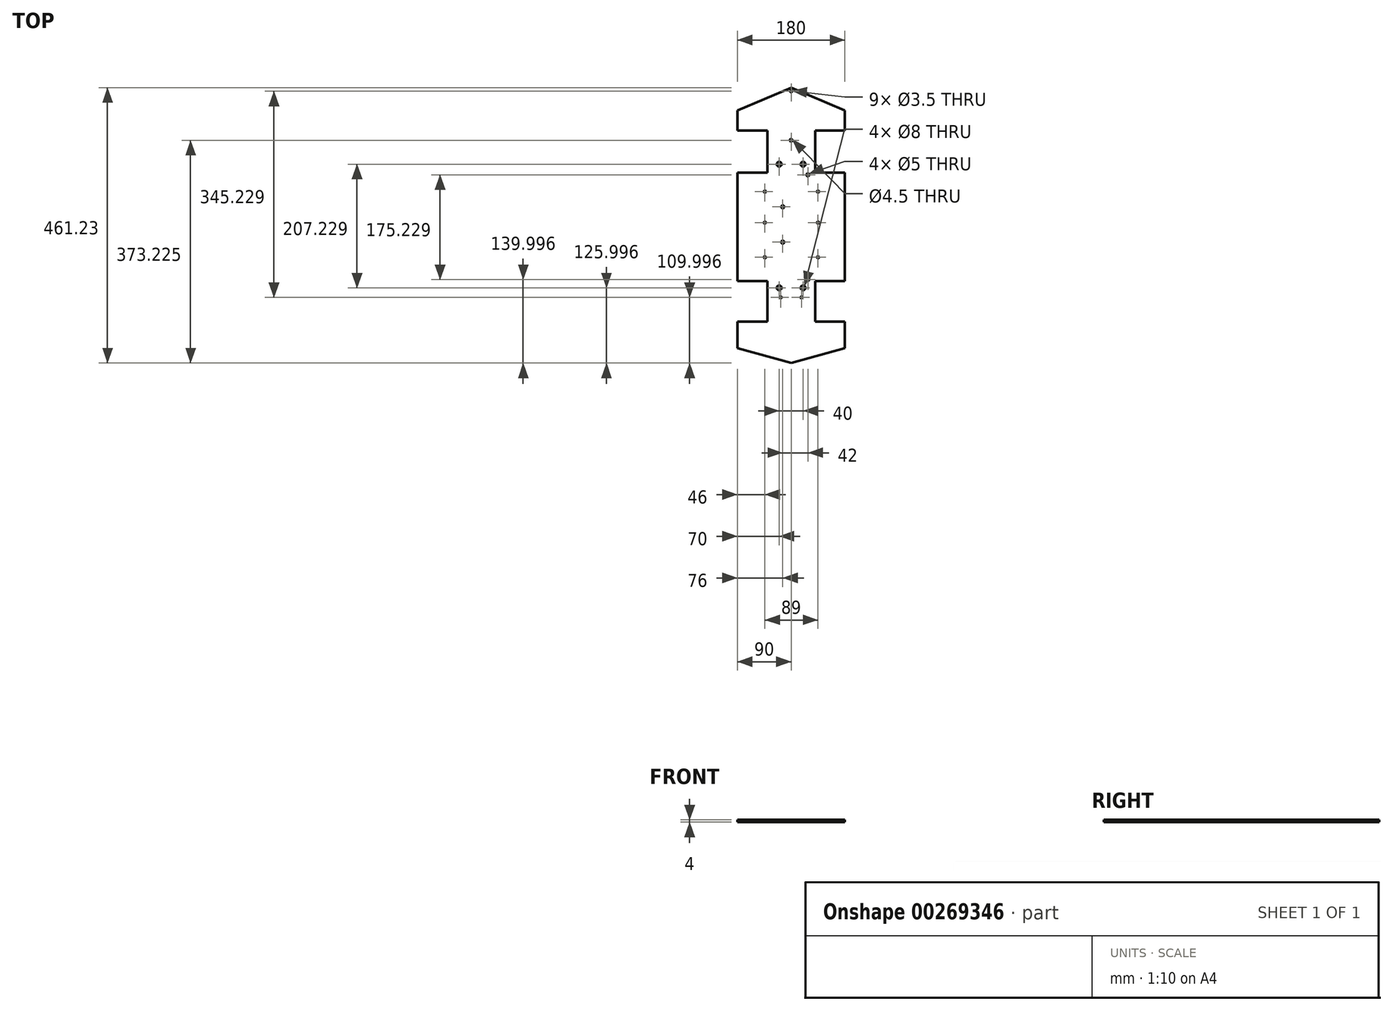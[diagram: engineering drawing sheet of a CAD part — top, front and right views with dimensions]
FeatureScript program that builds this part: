
annotation { "Feature Type Name" : "Feature", "Feature Type Description" : "" }
export const myFeature = defineFeature(function(context is Context, id is Id, definition is map)
    precondition{}
    {
        {
            var Q0;
            Q0=qCreatedBy(makeId("Top.planeOp"),FACE);
            var sketch = newSketch(context, id + "F0", { "sketchPlane" : qUnion([Q0])});
            skLineSegment(sketch, "E0", {"start": v(-90, -39.4) * mm, "end": v(-90, 51.6) * mm});
            skLineSegment(sketch, "E1", {"start": v(-90, -39.4) * mm, "end": v(-90, -130.4) * mm});
            skPoint(sketch, "E2.start.orphan", {"position": v(0, 0) * mm});
            skLineSegment(sketch, "E3", {"start": v(-90, 51.6) * mm, "end": v(-40, 51.6) * mm});
            skLineSegment(sketch, "E4", {"start": v(-40, 51.6) * mm, "end": v(-40, 121.6) * mm});
            skLineSegment(sketch, "E5", {"start": v(-40, 121.6) * mm, "end": v(-90, 121.6) * mm});
            skLineSegment(sketch, "E6", {"start": v(-90, 121.6) * mm, "end": v(-90, 155.6) * mm});
            skPoint(sketch, "E7.end.orphan", {"position": v(0, 220.82) * mm});
            skLineSegment(sketch, "E8", {"start": v(0, 190.54) * mm, "end": v(0, 193.6) * mm});
            skLineSegment(sketch, "E9", {"start": v(-90, 155.6) * mm, "end": v(0, 193.6) * mm});
            skLineSegment(sketch, "E10", {"start": v(-90, -130.4) * mm, "end": v(-40, -130.4) * mm});
            skLineSegment(sketch, "E11", {"start": v(-40, -130.4) * mm, "end": v(-40, -198.4) * mm});
            skLineSegment(sketch, "E12", {"start": v(-40, -198.4) * mm, "end": v(-90, -198.4) * mm});
            skLineSegment(sketch, "E13", {"start": v(-90, -198.4) * mm, "end": v(-90, -242.4) * mm});
            skLineSegment(sketch, "E14", {"start": v(-90, -242.4) * mm, "end": v(0, -267.62) * mm});
            skLineSegment(sketch, "E15", {"start": v(0, 193.6) * mm, "end": v(0, 190.54) * mm});
            skLineSegment(sketch, "E16.MirrorCS", {"start": v(90, 155.6) * mm, "end": v(0, 193.6) * mm});
            skLineSegment(sketch, "E17.MirrorCS", {"start": v(90, 121.6) * mm, "end": v(90, 155.6) * mm});
            skLineSegment(sketch, "E18.MirrorCS", {"start": v(40, 121.6) * mm, "end": v(90, 121.6) * mm});
            skLineSegment(sketch, "E19.MirrorCS", {"start": v(40, 51.6) * mm, "end": v(40, 121.6) * mm});
            skLineSegment(sketch, "E20.MirrorCS", {"start": v(90, 51.6) * mm, "end": v(40, 51.6) * mm});
            skLineSegment(sketch, "E21.MirrorCS", {"start": v(90, -39.4) * mm, "end": v(90, 51.6) * mm});
            skLineSegment(sketch, "E22.MirrorCS", {"start": v(90, -39.4) * mm, "end": v(90, -130.4) * mm});
            skLineSegment(sketch, "E23.MirrorCS", {"start": v(90, -130.4) * mm, "end": v(40, -130.4) * mm});
            skLineSegment(sketch, "E24.MirrorCS", {"start": v(40, -130.4) * mm, "end": v(40, -198.4) * mm});
            skLineSegment(sketch, "E25.MirrorCS", {"start": v(40, -198.4) * mm, "end": v(90, -198.4) * mm});
            skLineSegment(sketch, "E26.MirrorCS", {"start": v(90, -198.4) * mm, "end": v(90, -242.4) * mm});
            skLineSegment(sketch, "E27.MirrorCS", {"start": v(90, -242.4) * mm, "end": v(0, -267.62) * mm});
            skSolve(sketch);
        }
        {
            var Q0;
            Q0=makeQuery(id+"F0.imprint","IMPRINT",FACE,{"disambiguationData":[TD([[makeQuery(id+"F0.imprint","IMPRINT",EDGE,{"derivedFrom":sQuery(id+"F0.wireOp",EDGE,"E0")}),-1.0]])]});
            extrude(context, id + "F1", {"entities" : qUnion([Q0]), "depth" : 4 * mm});
        }
        {
            var Q0;
            Q0=makeQuery(id+"F1.opExtrude","CAP_FACE",FACE,{"disambiguationData":[OSD([sQuery(id+"F0.wireOp",EDGE,"E0"),sQuery(id+"F0.wireOp",EDGE,"E1"),sQuery(id+"F0.wireOp",EDGE,"E3"),sQuery(id+"F0.wireOp",EDGE,"E4"),sQuery(id+"F0.wireOp",EDGE,"E5"),sQuery(id+"F0.wireOp",EDGE,"E6"),sQuery(id+"F0.wireOp",EDGE,"E9"),sQuery(id+"F0.wireOp",EDGE,"E10"),sQuery(id+"F0.wireOp",EDGE,"E11"),sQuery(id+"F0.wireOp",EDGE,"E12"),sQuery(id+"F0.wireOp",EDGE,"E13"),sQuery(id+"F0.wireOp",EDGE,"E14"),sQuery(id+"F0.wireOp",EDGE,"E16.MirrorCS"),sQuery(id+"F0.wireOp",EDGE,"E17.MirrorCS"),sQuery(id+"F0.wireOp",EDGE,"E18.MirrorCS"),sQuery(id+"F0.wireOp",EDGE,"E19.MirrorCS"),sQuery(id+"F0.wireOp",EDGE,"E20.MirrorCS"),sQuery(id+"F0.wireOp",EDGE,"E21.MirrorCS"),sQuery(id+"F0.wireOp",EDGE,"E22.MirrorCS"),sQuery(id+"F0.wireOp",EDGE,"E23.MirrorCS"),sQuery(id+"F0.wireOp",EDGE,"E24.MirrorCS"),sQuery(id+"F0.wireOp",EDGE,"E25.MirrorCS"),sQuery(id+"F0.wireOp",EDGE,"E26.MirrorCS"),sQuery(id+"F0.wireOp",EDGE,"E27.MirrorCS")])],"isStart":false});
            var sketch = newSketch(context, id + "F2", { "sketchPlane" : qUnion([Q0])});
            skLineSegment(sketch, "E28", {"start": v(0, 193.6) * mm, "end": v(0, -267.62) * mm});
            skCircle(sketch, "E29", {"center": v(0, 187.6) * mm, "radius": 12.42 * mm});
            skSolve(sketch);
        }
        {
            var Q0;
            Q0=sQuery(id+"F2.wireOp",VERTEX,"E29.center");
            var Q1;
            Q1=makeQuery(id+"F1.opExtrude","SWEPT_BODY",BODY,{"disambiguationData":[OSD([sQuery(id+"F0.wireOp",EDGE,"E0"),sQuery(id+"F0.wireOp",EDGE,"E1"),sQuery(id+"F0.wireOp",EDGE,"E3"),sQuery(id+"F0.wireOp",EDGE,"E4"),sQuery(id+"F0.wireOp",EDGE,"E5"),sQuery(id+"F0.wireOp",EDGE,"E6"),sQuery(id+"F0.wireOp",EDGE,"E9"),sQuery(id+"F0.wireOp",EDGE,"E10"),sQuery(id+"F0.wireOp",EDGE,"E11"),sQuery(id+"F0.wireOp",EDGE,"E12"),sQuery(id+"F0.wireOp",EDGE,"E13"),sQuery(id+"F0.wireOp",EDGE,"E14"),sQuery(id+"F0.wireOp",EDGE,"E16.MirrorCS"),sQuery(id+"F0.wireOp",EDGE,"E17.MirrorCS"),sQuery(id+"F0.wireOp",EDGE,"E18.MirrorCS"),sQuery(id+"F0.wireOp",EDGE,"E19.MirrorCS"),sQuery(id+"F0.wireOp",EDGE,"E20.MirrorCS"),sQuery(id+"F0.wireOp",EDGE,"E21.MirrorCS"),sQuery(id+"F0.wireOp",EDGE,"E22.MirrorCS"),sQuery(id+"F0.wireOp",EDGE,"E23.MirrorCS"),sQuery(id+"F0.wireOp",EDGE,"E24.MirrorCS"),sQuery(id+"F0.wireOp",EDGE,"E25.MirrorCS"),sQuery(id+"F0.wireOp",EDGE,"E26.MirrorCS"),sQuery(id+"F0.wireOp",EDGE,"E27.MirrorCS")])]});
            hole(context, id + "F3", {"style" : HoleStyle.SIMPLE, "endStyle" : HoleEndStyle.BLIND, "holeDiameter" : 3.5 * mm, "holeDepth" : 4 * mm, "tappedDepth" : 12 * mm, "tapClearance" : 3, "startFromSketch" : true, "locations" : qUnion([Q0]), "scope" : qUnion([Q1])});
        }
        {
            var Q0;
            Q0=makeQuery(id+"F1.opExtrude","CAP_FACE",FACE,{"disambiguationData":[OSD([sQuery(id+"F0.wireOp",EDGE,"E0"),sQuery(id+"F0.wireOp",EDGE,"E1"),sQuery(id+"F0.wireOp",EDGE,"E3"),sQuery(id+"F0.wireOp",EDGE,"E4"),sQuery(id+"F0.wireOp",EDGE,"E5"),sQuery(id+"F0.wireOp",EDGE,"E6"),sQuery(id+"F0.wireOp",EDGE,"E9"),sQuery(id+"F0.wireOp",EDGE,"E10"),sQuery(id+"F0.wireOp",EDGE,"E11"),sQuery(id+"F0.wireOp",EDGE,"E12"),sQuery(id+"F0.wireOp",EDGE,"E13"),sQuery(id+"F0.wireOp",EDGE,"E14"),sQuery(id+"F0.wireOp",EDGE,"E16.MirrorCS"),sQuery(id+"F0.wireOp",EDGE,"E17.MirrorCS"),sQuery(id+"F0.wireOp",EDGE,"E18.MirrorCS"),sQuery(id+"F0.wireOp",EDGE,"E19.MirrorCS"),sQuery(id+"F0.wireOp",EDGE,"E20.MirrorCS"),sQuery(id+"F0.wireOp",EDGE,"E21.MirrorCS"),sQuery(id+"F0.wireOp",EDGE,"E22.MirrorCS"),sQuery(id+"F0.wireOp",EDGE,"E23.MirrorCS"),sQuery(id+"F0.wireOp",EDGE,"E24.MirrorCS"),sQuery(id+"F0.wireOp",EDGE,"E25.MirrorCS"),sQuery(id+"F0.wireOp",EDGE,"E26.MirrorCS"),sQuery(id+"F0.wireOp",EDGE,"E27.MirrorCS")])],"isStart":false});
            var sketch = newSketch(context, id + "F4", { "sketchPlane" : qUnion([Q0])});
            skLineSegment(sketch, "E30", {"start": v(0, 193.6) * mm, "end": v(0, -267.62) * mm});
            skCircle(sketch, "E31", {"center": v(0, 105.6) * mm, "radius": 11.78 * mm});
            skSolve(sketch);
        }
        {
            var Q0;
            Q0=sQuery(id+"F4.wireOp",VERTEX,"E31.center");
            var Q1;
            Q1=makeQuery(id+"F1.opExtrude","SWEPT_BODY",BODY,{"disambiguationData":[OSD([sQuery(id+"F0.wireOp",EDGE,"E0"),sQuery(id+"F0.wireOp",EDGE,"E1"),sQuery(id+"F0.wireOp",EDGE,"E3"),sQuery(id+"F0.wireOp",EDGE,"E4"),sQuery(id+"F0.wireOp",EDGE,"E5"),sQuery(id+"F0.wireOp",EDGE,"E6"),sQuery(id+"F0.wireOp",EDGE,"E9"),sQuery(id+"F0.wireOp",EDGE,"E10"),sQuery(id+"F0.wireOp",EDGE,"E11"),sQuery(id+"F0.wireOp",EDGE,"E12"),sQuery(id+"F0.wireOp",EDGE,"E13"),sQuery(id+"F0.wireOp",EDGE,"E14"),sQuery(id+"F0.wireOp",EDGE,"E16.MirrorCS"),sQuery(id+"F0.wireOp",EDGE,"E17.MirrorCS"),sQuery(id+"F0.wireOp",EDGE,"E18.MirrorCS"),sQuery(id+"F0.wireOp",EDGE,"E19.MirrorCS"),sQuery(id+"F0.wireOp",EDGE,"E20.MirrorCS"),sQuery(id+"F0.wireOp",EDGE,"E21.MirrorCS"),sQuery(id+"F0.wireOp",EDGE,"E22.MirrorCS"),sQuery(id+"F0.wireOp",EDGE,"E23.MirrorCS"),sQuery(id+"F0.wireOp",EDGE,"E24.MirrorCS"),sQuery(id+"F0.wireOp",EDGE,"E25.MirrorCS"),sQuery(id+"F0.wireOp",EDGE,"E26.MirrorCS"),sQuery(id+"F0.wireOp",EDGE,"E27.MirrorCS")])]});
            hole(context, id + "F5", {"style" : HoleStyle.SIMPLE, "endStyle" : HoleEndStyle.BLIND, "holeDiameter" : 4.5 * mm, "holeDepth" : 4 * mm, "tappedDepth" : 12 * mm, "tapClearance" : 3, "startFromSketch" : true, "locations" : qUnion([Q0]), "scope" : qUnion([Q1])});
        }
        {
            var Q0;
            Q0=makeQuery(id+"F1.opExtrude","CAP_FACE",FACE,{"disambiguationData":[OSD([sQuery(id+"F0.wireOp",EDGE,"E0"),sQuery(id+"F0.wireOp",EDGE,"E1"),sQuery(id+"F0.wireOp",EDGE,"E3"),sQuery(id+"F0.wireOp",EDGE,"E4"),sQuery(id+"F0.wireOp",EDGE,"E5"),sQuery(id+"F0.wireOp",EDGE,"E6"),sQuery(id+"F0.wireOp",EDGE,"E9"),sQuery(id+"F0.wireOp",EDGE,"E10"),sQuery(id+"F0.wireOp",EDGE,"E11"),sQuery(id+"F0.wireOp",EDGE,"E12"),sQuery(id+"F0.wireOp",EDGE,"E13"),sQuery(id+"F0.wireOp",EDGE,"E14"),sQuery(id+"F0.wireOp",EDGE,"E16.MirrorCS"),sQuery(id+"F0.wireOp",EDGE,"E17.MirrorCS"),sQuery(id+"F0.wireOp",EDGE,"E18.MirrorCS"),sQuery(id+"F0.wireOp",EDGE,"E19.MirrorCS"),sQuery(id+"F0.wireOp",EDGE,"E20.MirrorCS"),sQuery(id+"F0.wireOp",EDGE,"E21.MirrorCS"),sQuery(id+"F0.wireOp",EDGE,"E22.MirrorCS"),sQuery(id+"F0.wireOp",EDGE,"E23.MirrorCS"),sQuery(id+"F0.wireOp",EDGE,"E24.MirrorCS"),sQuery(id+"F0.wireOp",EDGE,"E25.MirrorCS"),sQuery(id+"F0.wireOp",EDGE,"E26.MirrorCS"),sQuery(id+"F0.wireOp",EDGE,"E27.MirrorCS")])],"isStart":false});
            var sketch = newSketch(context, id + "F6", { "sketchPlane" : qUnion([Q0])});
            skLineSegment(sketch, "E32", {"start": v(0, 193.6) * mm, "end": v(0, -267.62) * mm});
            skCircle(sketch, "E33", {"center": v(-20, 65.6) * mm, "radius": 13.57 * mm});
            skSolve(sketch);
        }
        {
            var Q0;
            Q0=sQuery(id+"F6.wireOp",VERTEX,"E33.center");
            var Q1;
            Q1=makeQuery(id+"F1.opExtrude","SWEPT_BODY",BODY,{"disambiguationData":[OSD([sQuery(id+"F0.wireOp",EDGE,"E0"),sQuery(id+"F0.wireOp",EDGE,"E1"),sQuery(id+"F0.wireOp",EDGE,"E3"),sQuery(id+"F0.wireOp",EDGE,"E4"),sQuery(id+"F0.wireOp",EDGE,"E5"),sQuery(id+"F0.wireOp",EDGE,"E6"),sQuery(id+"F0.wireOp",EDGE,"E9"),sQuery(id+"F0.wireOp",EDGE,"E10"),sQuery(id+"F0.wireOp",EDGE,"E11"),sQuery(id+"F0.wireOp",EDGE,"E12"),sQuery(id+"F0.wireOp",EDGE,"E13"),sQuery(id+"F0.wireOp",EDGE,"E14"),sQuery(id+"F0.wireOp",EDGE,"E16.MirrorCS"),sQuery(id+"F0.wireOp",EDGE,"E17.MirrorCS"),sQuery(id+"F0.wireOp",EDGE,"E18.MirrorCS"),sQuery(id+"F0.wireOp",EDGE,"E19.MirrorCS"),sQuery(id+"F0.wireOp",EDGE,"E20.MirrorCS"),sQuery(id+"F0.wireOp",EDGE,"E21.MirrorCS"),sQuery(id+"F0.wireOp",EDGE,"E22.MirrorCS"),sQuery(id+"F0.wireOp",EDGE,"E23.MirrorCS"),sQuery(id+"F0.wireOp",EDGE,"E24.MirrorCS"),sQuery(id+"F0.wireOp",EDGE,"E25.MirrorCS"),sQuery(id+"F0.wireOp",EDGE,"E26.MirrorCS"),sQuery(id+"F0.wireOp",EDGE,"E27.MirrorCS")])]});
            hole(context, id + "F7", {"style" : HoleStyle.SIMPLE, "endStyle" : HoleEndStyle.BLIND, "holeDiameter" : 8 * mm, "holeDepth" : 4 * mm, "tappedDepth" : 12 * mm, "tapClearance" : 3, "startFromSketch" : true, "locations" : qUnion([Q0]), "scope" : qUnion([Q1])});
        }
        {
            var Q0;
            Q0=makeQuery(id+"F1.opExtrude","CAP_FACE",FACE,{"disambiguationData":[OSD([sQuery(id+"F0.wireOp",EDGE,"E0"),sQuery(id+"F0.wireOp",EDGE,"E1"),sQuery(id+"F0.wireOp",EDGE,"E3"),sQuery(id+"F0.wireOp",EDGE,"E4"),sQuery(id+"F0.wireOp",EDGE,"E5"),sQuery(id+"F0.wireOp",EDGE,"E6"),sQuery(id+"F0.wireOp",EDGE,"E9"),sQuery(id+"F0.wireOp",EDGE,"E10"),sQuery(id+"F0.wireOp",EDGE,"E11"),sQuery(id+"F0.wireOp",EDGE,"E12"),sQuery(id+"F0.wireOp",EDGE,"E13"),sQuery(id+"F0.wireOp",EDGE,"E14"),sQuery(id+"F0.wireOp",EDGE,"E16.MirrorCS"),sQuery(id+"F0.wireOp",EDGE,"E17.MirrorCS"),sQuery(id+"F0.wireOp",EDGE,"E18.MirrorCS"),sQuery(id+"F0.wireOp",EDGE,"E19.MirrorCS"),sQuery(id+"F0.wireOp",EDGE,"E20.MirrorCS"),sQuery(id+"F0.wireOp",EDGE,"E21.MirrorCS"),sQuery(id+"F0.wireOp",EDGE,"E22.MirrorCS"),sQuery(id+"F0.wireOp",EDGE,"E23.MirrorCS"),sQuery(id+"F0.wireOp",EDGE,"E24.MirrorCS"),sQuery(id+"F0.wireOp",EDGE,"E25.MirrorCS"),sQuery(id+"F0.wireOp",EDGE,"E26.MirrorCS"),sQuery(id+"F0.wireOp",EDGE,"E27.MirrorCS")])],"isStart":false});
            var sketch = newSketch(context, id + "F8", { "sketchPlane" : qUnion([Q0])});
            skLineSegment(sketch, "E34", {"start": v(0, 193.6) * mm, "end": v(0, -267.62) * mm});
            skCircle(sketch, "E35", {"center": v(20, 65.6) * mm, "radius": 14.44 * mm});
            skSolve(sketch);
        }
        {
            var Q0;
            Q0=sQuery(id+"F8.wireOp",VERTEX,"E35.center");
            var Q1;
            Q1=makeQuery(id+"F1.opExtrude","SWEPT_BODY",BODY,{"disambiguationData":[OSD([sQuery(id+"F0.wireOp",EDGE,"E0"),sQuery(id+"F0.wireOp",EDGE,"E1"),sQuery(id+"F0.wireOp",EDGE,"E3"),sQuery(id+"F0.wireOp",EDGE,"E4"),sQuery(id+"F0.wireOp",EDGE,"E5"),sQuery(id+"F0.wireOp",EDGE,"E6"),sQuery(id+"F0.wireOp",EDGE,"E9"),sQuery(id+"F0.wireOp",EDGE,"E10"),sQuery(id+"F0.wireOp",EDGE,"E11"),sQuery(id+"F0.wireOp",EDGE,"E12"),sQuery(id+"F0.wireOp",EDGE,"E13"),sQuery(id+"F0.wireOp",EDGE,"E14"),sQuery(id+"F0.wireOp",EDGE,"E16.MirrorCS"),sQuery(id+"F0.wireOp",EDGE,"E17.MirrorCS"),sQuery(id+"F0.wireOp",EDGE,"E18.MirrorCS"),sQuery(id+"F0.wireOp",EDGE,"E19.MirrorCS"),sQuery(id+"F0.wireOp",EDGE,"E20.MirrorCS"),sQuery(id+"F0.wireOp",EDGE,"E21.MirrorCS"),sQuery(id+"F0.wireOp",EDGE,"E22.MirrorCS"),sQuery(id+"F0.wireOp",EDGE,"E23.MirrorCS"),sQuery(id+"F0.wireOp",EDGE,"E24.MirrorCS"),sQuery(id+"F0.wireOp",EDGE,"E25.MirrorCS"),sQuery(id+"F0.wireOp",EDGE,"E26.MirrorCS"),sQuery(id+"F0.wireOp",EDGE,"E27.MirrorCS")])]});
            hole(context, id + "F9", {"style" : HoleStyle.SIMPLE, "endStyle" : HoleEndStyle.BLIND, "holeDiameter" : 8 * mm, "holeDepth" : 4 * mm, "tappedDepth" : 12 * mm, "tapClearance" : 3, "startFromSketch" : true, "locations" : qUnion([Q0]), "scope" : qUnion([Q1])});
        }
        {
            var Q0;
            Q0=makeQuery(id+"F1.opExtrude","CAP_FACE",FACE,{"disambiguationData":[OSD([sQuery(id+"F0.wireOp",EDGE,"E0"),sQuery(id+"F0.wireOp",EDGE,"E1"),sQuery(id+"F0.wireOp",EDGE,"E3"),sQuery(id+"F0.wireOp",EDGE,"E4"),sQuery(id+"F0.wireOp",EDGE,"E5"),sQuery(id+"F0.wireOp",EDGE,"E6"),sQuery(id+"F0.wireOp",EDGE,"E9"),sQuery(id+"F0.wireOp",EDGE,"E10"),sQuery(id+"F0.wireOp",EDGE,"E11"),sQuery(id+"F0.wireOp",EDGE,"E12"),sQuery(id+"F0.wireOp",EDGE,"E13"),sQuery(id+"F0.wireOp",EDGE,"E14"),sQuery(id+"F0.wireOp",EDGE,"E16.MirrorCS"),sQuery(id+"F0.wireOp",EDGE,"E17.MirrorCS"),sQuery(id+"F0.wireOp",EDGE,"E18.MirrorCS"),sQuery(id+"F0.wireOp",EDGE,"E19.MirrorCS"),sQuery(id+"F0.wireOp",EDGE,"E20.MirrorCS"),sQuery(id+"F0.wireOp",EDGE,"E21.MirrorCS"),sQuery(id+"F0.wireOp",EDGE,"E22.MirrorCS"),sQuery(id+"F0.wireOp",EDGE,"E23.MirrorCS"),sQuery(id+"F0.wireOp",EDGE,"E24.MirrorCS"),sQuery(id+"F0.wireOp",EDGE,"E25.MirrorCS"),sQuery(id+"F0.wireOp",EDGE,"E26.MirrorCS"),sQuery(id+"F0.wireOp",EDGE,"E27.MirrorCS")])],"isStart":false});
            var sketch = newSketch(context, id + "F10", { "sketchPlane" : qUnion([Q0])});
            skLineSegment(sketch, "E36", {"start": v(0, 193.6) * mm, "end": v(0, -267.62) * mm});
            skCircle(sketch, "E37", {"center": v(28, 47.6) * mm, "radius": 46 * mm});
            skSolve(sketch);
        }
        {
            var Q0;
            Q0=sQuery(id+"F10.wireOp",VERTEX,"E37.center");
            var Q1;
            Q1=makeQuery(id+"F1.opExtrude","SWEPT_BODY",BODY,{"disambiguationData":[OSD([sQuery(id+"F0.wireOp",EDGE,"E0"),sQuery(id+"F0.wireOp",EDGE,"E1"),sQuery(id+"F0.wireOp",EDGE,"E3"),sQuery(id+"F0.wireOp",EDGE,"E4"),sQuery(id+"F0.wireOp",EDGE,"E5"),sQuery(id+"F0.wireOp",EDGE,"E6"),sQuery(id+"F0.wireOp",EDGE,"E9"),sQuery(id+"F0.wireOp",EDGE,"E10"),sQuery(id+"F0.wireOp",EDGE,"E11"),sQuery(id+"F0.wireOp",EDGE,"E12"),sQuery(id+"F0.wireOp",EDGE,"E13"),sQuery(id+"F0.wireOp",EDGE,"E14"),sQuery(id+"F0.wireOp",EDGE,"E16.MirrorCS"),sQuery(id+"F0.wireOp",EDGE,"E17.MirrorCS"),sQuery(id+"F0.wireOp",EDGE,"E18.MirrorCS"),sQuery(id+"F0.wireOp",EDGE,"E19.MirrorCS"),sQuery(id+"F0.wireOp",EDGE,"E20.MirrorCS"),sQuery(id+"F0.wireOp",EDGE,"E21.MirrorCS"),sQuery(id+"F0.wireOp",EDGE,"E22.MirrorCS"),sQuery(id+"F0.wireOp",EDGE,"E23.MirrorCS"),sQuery(id+"F0.wireOp",EDGE,"E24.MirrorCS"),sQuery(id+"F0.wireOp",EDGE,"E25.MirrorCS"),sQuery(id+"F0.wireOp",EDGE,"E26.MirrorCS"),sQuery(id+"F0.wireOp",EDGE,"E27.MirrorCS")])]});
            hole(context, id + "F11", {"style" : HoleStyle.SIMPLE, "endStyle" : HoleEndStyle.BLIND, "holeDiameter" : 5 * mm, "holeDepth" : 4 * mm, "tappedDepth" : 12 * mm, "tapClearance" : 3, "startFromSketch" : true, "locations" : qUnion([Q0]), "scope" : qUnion([Q1])});
        }
        {
            var Q0;
            Q0=makeQuery(id+"F1.opExtrude","CAP_FACE",FACE,{"disambiguationData":[OSD([sQuery(id+"F0.wireOp",EDGE,"E0"),sQuery(id+"F0.wireOp",EDGE,"E1"),sQuery(id+"F0.wireOp",EDGE,"E3"),sQuery(id+"F0.wireOp",EDGE,"E4"),sQuery(id+"F0.wireOp",EDGE,"E5"),sQuery(id+"F0.wireOp",EDGE,"E6"),sQuery(id+"F0.wireOp",EDGE,"E9"),sQuery(id+"F0.wireOp",EDGE,"E10"),sQuery(id+"F0.wireOp",EDGE,"E11"),sQuery(id+"F0.wireOp",EDGE,"E12"),sQuery(id+"F0.wireOp",EDGE,"E13"),sQuery(id+"F0.wireOp",EDGE,"E14"),sQuery(id+"F0.wireOp",EDGE,"E16.MirrorCS"),sQuery(id+"F0.wireOp",EDGE,"E17.MirrorCS"),sQuery(id+"F0.wireOp",EDGE,"E18.MirrorCS"),sQuery(id+"F0.wireOp",EDGE,"E19.MirrorCS"),sQuery(id+"F0.wireOp",EDGE,"E20.MirrorCS"),sQuery(id+"F0.wireOp",EDGE,"E21.MirrorCS"),sQuery(id+"F0.wireOp",EDGE,"E22.MirrorCS"),sQuery(id+"F0.wireOp",EDGE,"E23.MirrorCS"),sQuery(id+"F0.wireOp",EDGE,"E24.MirrorCS"),sQuery(id+"F0.wireOp",EDGE,"E25.MirrorCS"),sQuery(id+"F0.wireOp",EDGE,"E26.MirrorCS"),sQuery(id+"F0.wireOp",EDGE,"E27.MirrorCS")])],"isStart":false});
            var sketch = newSketch(context, id + "F12", { "sketchPlane" : qUnion([Q0])});
            skLineSegment(sketch, "E38", {"start": v(0, 193.6) * mm, "end": v(0, -267.62) * mm});
            skCircle(sketch, "E39", {"center": v(45, 19.6) * mm, "radius": 21.54 * mm});
            skSolve(sketch);
        }
        {
            var Q0;
            Q0=sQuery(id+"F12.wireOp",VERTEX,"E39.center");
            var Q1;
            Q1=makeQuery(id+"F1.opExtrude","SWEPT_BODY",BODY,{"disambiguationData":[OSD([sQuery(id+"F0.wireOp",EDGE,"E0"),sQuery(id+"F0.wireOp",EDGE,"E1"),sQuery(id+"F0.wireOp",EDGE,"E3"),sQuery(id+"F0.wireOp",EDGE,"E4"),sQuery(id+"F0.wireOp",EDGE,"E5"),sQuery(id+"F0.wireOp",EDGE,"E6"),sQuery(id+"F0.wireOp",EDGE,"E9"),sQuery(id+"F0.wireOp",EDGE,"E10"),sQuery(id+"F0.wireOp",EDGE,"E11"),sQuery(id+"F0.wireOp",EDGE,"E12"),sQuery(id+"F0.wireOp",EDGE,"E13"),sQuery(id+"F0.wireOp",EDGE,"E14"),sQuery(id+"F0.wireOp",EDGE,"E16.MirrorCS"),sQuery(id+"F0.wireOp",EDGE,"E17.MirrorCS"),sQuery(id+"F0.wireOp",EDGE,"E18.MirrorCS"),sQuery(id+"F0.wireOp",EDGE,"E19.MirrorCS"),sQuery(id+"F0.wireOp",EDGE,"E20.MirrorCS"),sQuery(id+"F0.wireOp",EDGE,"E21.MirrorCS"),sQuery(id+"F0.wireOp",EDGE,"E22.MirrorCS"),sQuery(id+"F0.wireOp",EDGE,"E23.MirrorCS"),sQuery(id+"F0.wireOp",EDGE,"E24.MirrorCS"),sQuery(id+"F0.wireOp",EDGE,"E25.MirrorCS"),sQuery(id+"F0.wireOp",EDGE,"E26.MirrorCS"),sQuery(id+"F0.wireOp",EDGE,"E27.MirrorCS")])]});
            hole(context, id + "F13", {"style" : HoleStyle.SIMPLE, "endStyle" : HoleEndStyle.BLIND, "holeDiameter" : 3.5 * mm, "holeDepth" : 4 * mm, "tappedDepth" : 12 * mm, "tapClearance" : 3, "startFromSketch" : true, "locations" : qUnion([Q0]), "scope" : qUnion([Q1])});
        }
        {
            var Q0;
            Q0=makeQuery(id+"F1.opExtrude","CAP_FACE",FACE,{"disambiguationData":[OSD([sQuery(id+"F0.wireOp",EDGE,"E0"),sQuery(id+"F0.wireOp",EDGE,"E1"),sQuery(id+"F0.wireOp",EDGE,"E3"),sQuery(id+"F0.wireOp",EDGE,"E4"),sQuery(id+"F0.wireOp",EDGE,"E5"),sQuery(id+"F0.wireOp",EDGE,"E6"),sQuery(id+"F0.wireOp",EDGE,"E9"),sQuery(id+"F0.wireOp",EDGE,"E10"),sQuery(id+"F0.wireOp",EDGE,"E11"),sQuery(id+"F0.wireOp",EDGE,"E12"),sQuery(id+"F0.wireOp",EDGE,"E13"),sQuery(id+"F0.wireOp",EDGE,"E14"),sQuery(id+"F0.wireOp",EDGE,"E16.MirrorCS"),sQuery(id+"F0.wireOp",EDGE,"E17.MirrorCS"),sQuery(id+"F0.wireOp",EDGE,"E18.MirrorCS"),sQuery(id+"F0.wireOp",EDGE,"E19.MirrorCS"),sQuery(id+"F0.wireOp",EDGE,"E20.MirrorCS"),sQuery(id+"F0.wireOp",EDGE,"E21.MirrorCS"),sQuery(id+"F0.wireOp",EDGE,"E22.MirrorCS"),sQuery(id+"F0.wireOp",EDGE,"E23.MirrorCS"),sQuery(id+"F0.wireOp",EDGE,"E24.MirrorCS"),sQuery(id+"F0.wireOp",EDGE,"E25.MirrorCS"),sQuery(id+"F0.wireOp",EDGE,"E26.MirrorCS"),sQuery(id+"F0.wireOp",EDGE,"E27.MirrorCS")])],"isStart":false});
            var sketch = newSketch(context, id + "F14", { "sketchPlane" : qUnion([Q0])});
            skLineSegment(sketch, "E40", {"start": v(0, 193.6) * mm, "end": v(0, -267.62) * mm});
            skCircle(sketch, "E41", {"center": v(45, -32.4) * mm, "radius": 23.3 * mm});
            skSolve(sketch);
        }
        {
            var Q0;
            Q0=sQuery(id+"F14.wireOp",VERTEX,"E41.center");
            var Q1;
            Q1=makeQuery(id+"F1.opExtrude","SWEPT_BODY",BODY,{"disambiguationData":[OSD([sQuery(id+"F0.wireOp",EDGE,"E0"),sQuery(id+"F0.wireOp",EDGE,"E1"),sQuery(id+"F0.wireOp",EDGE,"E3"),sQuery(id+"F0.wireOp",EDGE,"E4"),sQuery(id+"F0.wireOp",EDGE,"E5"),sQuery(id+"F0.wireOp",EDGE,"E6"),sQuery(id+"F0.wireOp",EDGE,"E9"),sQuery(id+"F0.wireOp",EDGE,"E10"),sQuery(id+"F0.wireOp",EDGE,"E11"),sQuery(id+"F0.wireOp",EDGE,"E12"),sQuery(id+"F0.wireOp",EDGE,"E13"),sQuery(id+"F0.wireOp",EDGE,"E14"),sQuery(id+"F0.wireOp",EDGE,"E16.MirrorCS"),sQuery(id+"F0.wireOp",EDGE,"E17.MirrorCS"),sQuery(id+"F0.wireOp",EDGE,"E18.MirrorCS"),sQuery(id+"F0.wireOp",EDGE,"E19.MirrorCS"),sQuery(id+"F0.wireOp",EDGE,"E20.MirrorCS"),sQuery(id+"F0.wireOp",EDGE,"E21.MirrorCS"),sQuery(id+"F0.wireOp",EDGE,"E22.MirrorCS"),sQuery(id+"F0.wireOp",EDGE,"E23.MirrorCS"),sQuery(id+"F0.wireOp",EDGE,"E24.MirrorCS"),sQuery(id+"F0.wireOp",EDGE,"E25.MirrorCS"),sQuery(id+"F0.wireOp",EDGE,"E26.MirrorCS"),sQuery(id+"F0.wireOp",EDGE,"E27.MirrorCS")])]});
            hole(context, id + "F15", {"style" : HoleStyle.SIMPLE, "endStyle" : HoleEndStyle.BLIND, "holeDiameter" : 3.5 * mm, "holeDepth" : 4 * mm, "tappedDepth" : 12 * mm, "tapClearance" : 3, "startFromSketch" : true, "locations" : qUnion([Q0]), "scope" : qUnion([Q1])});
        }
        {
            var Q0;
            Q0=makeQuery(id+"F1.opExtrude","CAP_FACE",FACE,{"disambiguationData":[OSD([sQuery(id+"F0.wireOp",EDGE,"E0"),sQuery(id+"F0.wireOp",EDGE,"E1"),sQuery(id+"F0.wireOp",EDGE,"E3"),sQuery(id+"F0.wireOp",EDGE,"E4"),sQuery(id+"F0.wireOp",EDGE,"E5"),sQuery(id+"F0.wireOp",EDGE,"E6"),sQuery(id+"F0.wireOp",EDGE,"E9"),sQuery(id+"F0.wireOp",EDGE,"E10"),sQuery(id+"F0.wireOp",EDGE,"E11"),sQuery(id+"F0.wireOp",EDGE,"E12"),sQuery(id+"F0.wireOp",EDGE,"E13"),sQuery(id+"F0.wireOp",EDGE,"E14"),sQuery(id+"F0.wireOp",EDGE,"E16.MirrorCS"),sQuery(id+"F0.wireOp",EDGE,"E17.MirrorCS"),sQuery(id+"F0.wireOp",EDGE,"E18.MirrorCS"),sQuery(id+"F0.wireOp",EDGE,"E19.MirrorCS"),sQuery(id+"F0.wireOp",EDGE,"E20.MirrorCS"),sQuery(id+"F0.wireOp",EDGE,"E21.MirrorCS"),sQuery(id+"F0.wireOp",EDGE,"E22.MirrorCS"),sQuery(id+"F0.wireOp",EDGE,"E23.MirrorCS"),sQuery(id+"F0.wireOp",EDGE,"E24.MirrorCS"),sQuery(id+"F0.wireOp",EDGE,"E25.MirrorCS"),sQuery(id+"F0.wireOp",EDGE,"E26.MirrorCS"),sQuery(id+"F0.wireOp",EDGE,"E27.MirrorCS")])],"isStart":false});
            var sketch = newSketch(context, id + "F16", { "sketchPlane" : qUnion([Q0])});
            skLineSegment(sketch, "E42", {"start": v(0, 193.6) * mm, "end": v(0, -267.62) * mm});
            skCircle(sketch, "E43", {"center": v(45, -90.4) * mm, "radius": 22.73 * mm});
            skSolve(sketch);
        }
        {
            var Q0;
            Q0=sQuery(id+"F16.wireOp",VERTEX,"E43.center");
            var Q1;
            Q1=makeQuery(id+"F1.opExtrude","SWEPT_BODY",BODY,{"disambiguationData":[OSD([sQuery(id+"F0.wireOp",EDGE,"E0"),sQuery(id+"F0.wireOp",EDGE,"E1"),sQuery(id+"F0.wireOp",EDGE,"E3"),sQuery(id+"F0.wireOp",EDGE,"E4"),sQuery(id+"F0.wireOp",EDGE,"E5"),sQuery(id+"F0.wireOp",EDGE,"E6"),sQuery(id+"F0.wireOp",EDGE,"E9"),sQuery(id+"F0.wireOp",EDGE,"E10"),sQuery(id+"F0.wireOp",EDGE,"E11"),sQuery(id+"F0.wireOp",EDGE,"E12"),sQuery(id+"F0.wireOp",EDGE,"E13"),sQuery(id+"F0.wireOp",EDGE,"E14"),sQuery(id+"F0.wireOp",EDGE,"E16.MirrorCS"),sQuery(id+"F0.wireOp",EDGE,"E17.MirrorCS"),sQuery(id+"F0.wireOp",EDGE,"E18.MirrorCS"),sQuery(id+"F0.wireOp",EDGE,"E19.MirrorCS"),sQuery(id+"F0.wireOp",EDGE,"E20.MirrorCS"),sQuery(id+"F0.wireOp",EDGE,"E21.MirrorCS"),sQuery(id+"F0.wireOp",EDGE,"E22.MirrorCS"),sQuery(id+"F0.wireOp",EDGE,"E23.MirrorCS"),sQuery(id+"F0.wireOp",EDGE,"E24.MirrorCS"),sQuery(id+"F0.wireOp",EDGE,"E25.MirrorCS"),sQuery(id+"F0.wireOp",EDGE,"E26.MirrorCS"),sQuery(id+"F0.wireOp",EDGE,"E27.MirrorCS")])]});
            hole(context, id + "F17", {"style" : HoleStyle.SIMPLE, "endStyle" : HoleEndStyle.BLIND, "holeDiameter" : 3.5 * mm, "holeDepth" : 4 * mm, "tappedDepth" : 12 * mm, "tapClearance" : 3, "startFromSketch" : true, "locations" : qUnion([Q0]), "scope" : qUnion([Q1])});
        }
        {
            var Q0;
            Q0=makeQuery(id+"F1.opExtrude","CAP_FACE",FACE,{"disambiguationData":[OSD([sQuery(id+"F0.wireOp",EDGE,"E0"),sQuery(id+"F0.wireOp",EDGE,"E1"),sQuery(id+"F0.wireOp",EDGE,"E3"),sQuery(id+"F0.wireOp",EDGE,"E4"),sQuery(id+"F0.wireOp",EDGE,"E5"),sQuery(id+"F0.wireOp",EDGE,"E6"),sQuery(id+"F0.wireOp",EDGE,"E9"),sQuery(id+"F0.wireOp",EDGE,"E10"),sQuery(id+"F0.wireOp",EDGE,"E11"),sQuery(id+"F0.wireOp",EDGE,"E12"),sQuery(id+"F0.wireOp",EDGE,"E13"),sQuery(id+"F0.wireOp",EDGE,"E14"),sQuery(id+"F0.wireOp",EDGE,"E16.MirrorCS"),sQuery(id+"F0.wireOp",EDGE,"E17.MirrorCS"),sQuery(id+"F0.wireOp",EDGE,"E18.MirrorCS"),sQuery(id+"F0.wireOp",EDGE,"E19.MirrorCS"),sQuery(id+"F0.wireOp",EDGE,"E20.MirrorCS"),sQuery(id+"F0.wireOp",EDGE,"E21.MirrorCS"),sQuery(id+"F0.wireOp",EDGE,"E22.MirrorCS"),sQuery(id+"F0.wireOp",EDGE,"E23.MirrorCS"),sQuery(id+"F0.wireOp",EDGE,"E24.MirrorCS"),sQuery(id+"F0.wireOp",EDGE,"E25.MirrorCS"),sQuery(id+"F0.wireOp",EDGE,"E26.MirrorCS"),sQuery(id+"F0.wireOp",EDGE,"E27.MirrorCS")])],"isStart":false});
            var sketch = newSketch(context, id + "F18", { "sketchPlane" : qUnion([Q0])});
            skLineSegment(sketch, "E44", {"start": v(0, 193.6) * mm, "end": v(0, -267.62) * mm});
            skCircle(sketch, "E45", {"center": v(-44, 19.6) * mm, "radius": 18.1 * mm});
            skSolve(sketch);
        }
        {
            var Q0;
            Q0=sQuery(id+"F18.wireOp",VERTEX,"E45.center");
            var Q1;
            Q1=makeQuery(id+"F1.opExtrude","SWEPT_BODY",BODY,{"disambiguationData":[OSD([sQuery(id+"F0.wireOp",EDGE,"E0"),sQuery(id+"F0.wireOp",EDGE,"E1"),sQuery(id+"F0.wireOp",EDGE,"E3"),sQuery(id+"F0.wireOp",EDGE,"E4"),sQuery(id+"F0.wireOp",EDGE,"E5"),sQuery(id+"F0.wireOp",EDGE,"E6"),sQuery(id+"F0.wireOp",EDGE,"E9"),sQuery(id+"F0.wireOp",EDGE,"E10"),sQuery(id+"F0.wireOp",EDGE,"E11"),sQuery(id+"F0.wireOp",EDGE,"E12"),sQuery(id+"F0.wireOp",EDGE,"E13"),sQuery(id+"F0.wireOp",EDGE,"E14"),sQuery(id+"F0.wireOp",EDGE,"E16.MirrorCS"),sQuery(id+"F0.wireOp",EDGE,"E17.MirrorCS"),sQuery(id+"F0.wireOp",EDGE,"E18.MirrorCS"),sQuery(id+"F0.wireOp",EDGE,"E19.MirrorCS"),sQuery(id+"F0.wireOp",EDGE,"E20.MirrorCS"),sQuery(id+"F0.wireOp",EDGE,"E21.MirrorCS"),sQuery(id+"F0.wireOp",EDGE,"E22.MirrorCS"),sQuery(id+"F0.wireOp",EDGE,"E23.MirrorCS"),sQuery(id+"F0.wireOp",EDGE,"E24.MirrorCS"),sQuery(id+"F0.wireOp",EDGE,"E25.MirrorCS"),sQuery(id+"F0.wireOp",EDGE,"E26.MirrorCS"),sQuery(id+"F0.wireOp",EDGE,"E27.MirrorCS")])]});
            hole(context, id + "F19", {"style" : HoleStyle.SIMPLE, "endStyle" : HoleEndStyle.BLIND, "holeDiameter" : 3.5 * mm, "holeDepth" : 4 * mm, "tappedDepth" : 12 * mm, "tapClearance" : 3, "startFromSketch" : true, "locations" : qUnion([Q0]), "scope" : qUnion([Q1])});
        }
        {
            var Q0;
            Q0=makeQuery(id+"F1.opExtrude","CAP_FACE",FACE,{"disambiguationData":[OSD([sQuery(id+"F0.wireOp",EDGE,"E0"),sQuery(id+"F0.wireOp",EDGE,"E1"),sQuery(id+"F0.wireOp",EDGE,"E3"),sQuery(id+"F0.wireOp",EDGE,"E4"),sQuery(id+"F0.wireOp",EDGE,"E5"),sQuery(id+"F0.wireOp",EDGE,"E6"),sQuery(id+"F0.wireOp",EDGE,"E9"),sQuery(id+"F0.wireOp",EDGE,"E10"),sQuery(id+"F0.wireOp",EDGE,"E11"),sQuery(id+"F0.wireOp",EDGE,"E12"),sQuery(id+"F0.wireOp",EDGE,"E13"),sQuery(id+"F0.wireOp",EDGE,"E14"),sQuery(id+"F0.wireOp",EDGE,"E16.MirrorCS"),sQuery(id+"F0.wireOp",EDGE,"E17.MirrorCS"),sQuery(id+"F0.wireOp",EDGE,"E18.MirrorCS"),sQuery(id+"F0.wireOp",EDGE,"E19.MirrorCS"),sQuery(id+"F0.wireOp",EDGE,"E20.MirrorCS"),sQuery(id+"F0.wireOp",EDGE,"E21.MirrorCS"),sQuery(id+"F0.wireOp",EDGE,"E22.MirrorCS"),sQuery(id+"F0.wireOp",EDGE,"E23.MirrorCS"),sQuery(id+"F0.wireOp",EDGE,"E24.MirrorCS"),sQuery(id+"F0.wireOp",EDGE,"E25.MirrorCS"),sQuery(id+"F0.wireOp",EDGE,"E26.MirrorCS"),sQuery(id+"F0.wireOp",EDGE,"E27.MirrorCS")])],"isStart":false});
            var sketch = newSketch(context, id + "F20", { "sketchPlane" : qUnion([Q0])});
            skLineSegment(sketch, "E46", {"start": v(0, 193.6) * mm, "end": v(0, -267.62) * mm});
            skCircle(sketch, "E47", {"center": v(-44, -32.4) * mm, "radius": 29.37 * mm});
            skSolve(sketch);
        }
        {
            var Q0;
            Q0=sQuery(id+"F20.wireOp",VERTEX,"E47.center");
            var Q1;
            Q1=makeQuery(id+"F1.opExtrude","SWEPT_BODY",BODY,{"disambiguationData":[OSD([sQuery(id+"F0.wireOp",EDGE,"E0"),sQuery(id+"F0.wireOp",EDGE,"E1"),sQuery(id+"F0.wireOp",EDGE,"E3"),sQuery(id+"F0.wireOp",EDGE,"E4"),sQuery(id+"F0.wireOp",EDGE,"E5"),sQuery(id+"F0.wireOp",EDGE,"E6"),sQuery(id+"F0.wireOp",EDGE,"E9"),sQuery(id+"F0.wireOp",EDGE,"E10"),sQuery(id+"F0.wireOp",EDGE,"E11"),sQuery(id+"F0.wireOp",EDGE,"E12"),sQuery(id+"F0.wireOp",EDGE,"E13"),sQuery(id+"F0.wireOp",EDGE,"E14"),sQuery(id+"F0.wireOp",EDGE,"E16.MirrorCS"),sQuery(id+"F0.wireOp",EDGE,"E17.MirrorCS"),sQuery(id+"F0.wireOp",EDGE,"E18.MirrorCS"),sQuery(id+"F0.wireOp",EDGE,"E19.MirrorCS"),sQuery(id+"F0.wireOp",EDGE,"E20.MirrorCS"),sQuery(id+"F0.wireOp",EDGE,"E21.MirrorCS"),sQuery(id+"F0.wireOp",EDGE,"E22.MirrorCS"),sQuery(id+"F0.wireOp",EDGE,"E23.MirrorCS"),sQuery(id+"F0.wireOp",EDGE,"E24.MirrorCS"),sQuery(id+"F0.wireOp",EDGE,"E25.MirrorCS"),sQuery(id+"F0.wireOp",EDGE,"E26.MirrorCS"),sQuery(id+"F0.wireOp",EDGE,"E27.MirrorCS")])]});
            hole(context, id + "F21", {"style" : HoleStyle.SIMPLE, "endStyle" : HoleEndStyle.BLIND, "holeDiameter" : 3.5 * mm, "holeDepth" : 4 * mm, "tappedDepth" : 12 * mm, "tapClearance" : 3, "startFromSketch" : true, "locations" : qUnion([Q0]), "scope" : qUnion([Q1])});
        }
        {
            var Q0;
            Q0=makeQuery(id+"F1.opExtrude","CAP_FACE",FACE,{"disambiguationData":[OSD([sQuery(id+"F0.wireOp",EDGE,"E0"),sQuery(id+"F0.wireOp",EDGE,"E1"),sQuery(id+"F0.wireOp",EDGE,"E3"),sQuery(id+"F0.wireOp",EDGE,"E4"),sQuery(id+"F0.wireOp",EDGE,"E5"),sQuery(id+"F0.wireOp",EDGE,"E6"),sQuery(id+"F0.wireOp",EDGE,"E9"),sQuery(id+"F0.wireOp",EDGE,"E10"),sQuery(id+"F0.wireOp",EDGE,"E11"),sQuery(id+"F0.wireOp",EDGE,"E12"),sQuery(id+"F0.wireOp",EDGE,"E13"),sQuery(id+"F0.wireOp",EDGE,"E14"),sQuery(id+"F0.wireOp",EDGE,"E16.MirrorCS"),sQuery(id+"F0.wireOp",EDGE,"E17.MirrorCS"),sQuery(id+"F0.wireOp",EDGE,"E18.MirrorCS"),sQuery(id+"F0.wireOp",EDGE,"E19.MirrorCS"),sQuery(id+"F0.wireOp",EDGE,"E20.MirrorCS"),sQuery(id+"F0.wireOp",EDGE,"E21.MirrorCS"),sQuery(id+"F0.wireOp",EDGE,"E22.MirrorCS"),sQuery(id+"F0.wireOp",EDGE,"E23.MirrorCS"),sQuery(id+"F0.wireOp",EDGE,"E24.MirrorCS"),sQuery(id+"F0.wireOp",EDGE,"E25.MirrorCS"),sQuery(id+"F0.wireOp",EDGE,"E26.MirrorCS"),sQuery(id+"F0.wireOp",EDGE,"E27.MirrorCS")])],"isStart":false});
            var sketch = newSketch(context, id + "F22", { "sketchPlane" : qUnion([Q0])});
            skLineSegment(sketch, "E48", {"start": v(0, 193.6) * mm, "end": v(0, -267.62) * mm});
            skCircle(sketch, "E49", {"center": v(-44, -90.4) * mm, "radius": 19.7 * mm});
            skSolve(sketch);
        }
        {
            var Q0;
            Q0=sQuery(id+"F22.wireOp",VERTEX,"E49.center");
            var Q1;
            Q1=makeQuery(id+"F1.opExtrude","SWEPT_BODY",BODY,{"disambiguationData":[OSD([sQuery(id+"F0.wireOp",EDGE,"E0"),sQuery(id+"F0.wireOp",EDGE,"E1"),sQuery(id+"F0.wireOp",EDGE,"E3"),sQuery(id+"F0.wireOp",EDGE,"E4"),sQuery(id+"F0.wireOp",EDGE,"E5"),sQuery(id+"F0.wireOp",EDGE,"E6"),sQuery(id+"F0.wireOp",EDGE,"E9"),sQuery(id+"F0.wireOp",EDGE,"E10"),sQuery(id+"F0.wireOp",EDGE,"E11"),sQuery(id+"F0.wireOp",EDGE,"E12"),sQuery(id+"F0.wireOp",EDGE,"E13"),sQuery(id+"F0.wireOp",EDGE,"E14"),sQuery(id+"F0.wireOp",EDGE,"E16.MirrorCS"),sQuery(id+"F0.wireOp",EDGE,"E17.MirrorCS"),sQuery(id+"F0.wireOp",EDGE,"E18.MirrorCS"),sQuery(id+"F0.wireOp",EDGE,"E19.MirrorCS"),sQuery(id+"F0.wireOp",EDGE,"E20.MirrorCS"),sQuery(id+"F0.wireOp",EDGE,"E21.MirrorCS"),sQuery(id+"F0.wireOp",EDGE,"E22.MirrorCS"),sQuery(id+"F0.wireOp",EDGE,"E23.MirrorCS"),sQuery(id+"F0.wireOp",EDGE,"E24.MirrorCS"),sQuery(id+"F0.wireOp",EDGE,"E25.MirrorCS"),sQuery(id+"F0.wireOp",EDGE,"E26.MirrorCS"),sQuery(id+"F0.wireOp",EDGE,"E27.MirrorCS")])]});
            hole(context, id + "F23", {"style" : HoleStyle.SIMPLE, "endStyle" : HoleEndStyle.BLIND, "holeDiameter" : 3.5 * mm, "holeDepth" : 4 * mm, "tappedDepth" : 12 * mm, "tapClearance" : 3, "startFromSketch" : true, "locations" : qUnion([Q0]), "scope" : qUnion([Q1])});
        }
        {
            var Q0;
            Q0=makeQuery(id+"F1.opExtrude","CAP_FACE",FACE,{"disambiguationData":[OSD([sQuery(id+"F0.wireOp",EDGE,"E0"),sQuery(id+"F0.wireOp",EDGE,"E1"),sQuery(id+"F0.wireOp",EDGE,"E3"),sQuery(id+"F0.wireOp",EDGE,"E4"),sQuery(id+"F0.wireOp",EDGE,"E5"),sQuery(id+"F0.wireOp",EDGE,"E6"),sQuery(id+"F0.wireOp",EDGE,"E9"),sQuery(id+"F0.wireOp",EDGE,"E10"),sQuery(id+"F0.wireOp",EDGE,"E11"),sQuery(id+"F0.wireOp",EDGE,"E12"),sQuery(id+"F0.wireOp",EDGE,"E13"),sQuery(id+"F0.wireOp",EDGE,"E14"),sQuery(id+"F0.wireOp",EDGE,"E16.MirrorCS"),sQuery(id+"F0.wireOp",EDGE,"E17.MirrorCS"),sQuery(id+"F0.wireOp",EDGE,"E18.MirrorCS"),sQuery(id+"F0.wireOp",EDGE,"E19.MirrorCS"),sQuery(id+"F0.wireOp",EDGE,"E20.MirrorCS"),sQuery(id+"F0.wireOp",EDGE,"E21.MirrorCS"),sQuery(id+"F0.wireOp",EDGE,"E22.MirrorCS"),sQuery(id+"F0.wireOp",EDGE,"E23.MirrorCS"),sQuery(id+"F0.wireOp",EDGE,"E24.MirrorCS"),sQuery(id+"F0.wireOp",EDGE,"E25.MirrorCS"),sQuery(id+"F0.wireOp",EDGE,"E26.MirrorCS"),sQuery(id+"F0.wireOp",EDGE,"E27.MirrorCS")])],"isStart":false});
            var sketch = newSketch(context, id + "F24", { "sketchPlane" : qUnion([Q0])});
            skLineSegment(sketch, "E50", {"start": v(0, 193.6) * mm, "end": v(0, -267.62) * mm});
            skCircle(sketch, "E51", {"center": v(-14, -5.9) * mm, "radius": 23.67 * mm});
            skSolve(sketch);
        }
        {
            var Q0;
            Q0=sQuery(id+"F24.wireOp",VERTEX,"E51.center");
            var Q1;
            Q1=makeQuery(id+"F1.opExtrude","SWEPT_BODY",BODY,{"disambiguationData":[OSD([sQuery(id+"F0.wireOp",EDGE,"E0"),sQuery(id+"F0.wireOp",EDGE,"E1"),sQuery(id+"F0.wireOp",EDGE,"E3"),sQuery(id+"F0.wireOp",EDGE,"E4"),sQuery(id+"F0.wireOp",EDGE,"E5"),sQuery(id+"F0.wireOp",EDGE,"E6"),sQuery(id+"F0.wireOp",EDGE,"E9"),sQuery(id+"F0.wireOp",EDGE,"E10"),sQuery(id+"F0.wireOp",EDGE,"E11"),sQuery(id+"F0.wireOp",EDGE,"E12"),sQuery(id+"F0.wireOp",EDGE,"E13"),sQuery(id+"F0.wireOp",EDGE,"E14"),sQuery(id+"F0.wireOp",EDGE,"E16.MirrorCS"),sQuery(id+"F0.wireOp",EDGE,"E17.MirrorCS"),sQuery(id+"F0.wireOp",EDGE,"E18.MirrorCS"),sQuery(id+"F0.wireOp",EDGE,"E19.MirrorCS"),sQuery(id+"F0.wireOp",EDGE,"E20.MirrorCS"),sQuery(id+"F0.wireOp",EDGE,"E21.MirrorCS"),sQuery(id+"F0.wireOp",EDGE,"E22.MirrorCS"),sQuery(id+"F0.wireOp",EDGE,"E23.MirrorCS"),sQuery(id+"F0.wireOp",EDGE,"E24.MirrorCS"),sQuery(id+"F0.wireOp",EDGE,"E25.MirrorCS"),sQuery(id+"F0.wireOp",EDGE,"E26.MirrorCS"),sQuery(id+"F0.wireOp",EDGE,"E27.MirrorCS")])]});
            hole(context, id + "F25", {"style" : HoleStyle.SIMPLE, "endStyle" : HoleEndStyle.BLIND, "holeDiameter" : 5 * mm, "holeDepth" : 4 * mm, "tappedDepth" : 12 * mm, "tapClearance" : 3, "startFromSketch" : true, "locations" : qUnion([Q0]), "scope" : qUnion([Q1])});
        }
        {
            var Q0;
            Q0=makeQuery(id+"F1.opExtrude","CAP_FACE",FACE,{"disambiguationData":[OSD([sQuery(id+"F0.wireOp",EDGE,"E0"),sQuery(id+"F0.wireOp",EDGE,"E1"),sQuery(id+"F0.wireOp",EDGE,"E3"),sQuery(id+"F0.wireOp",EDGE,"E4"),sQuery(id+"F0.wireOp",EDGE,"E5"),sQuery(id+"F0.wireOp",EDGE,"E6"),sQuery(id+"F0.wireOp",EDGE,"E9"),sQuery(id+"F0.wireOp",EDGE,"E10"),sQuery(id+"F0.wireOp",EDGE,"E11"),sQuery(id+"F0.wireOp",EDGE,"E12"),sQuery(id+"F0.wireOp",EDGE,"E13"),sQuery(id+"F0.wireOp",EDGE,"E14"),sQuery(id+"F0.wireOp",EDGE,"E16.MirrorCS"),sQuery(id+"F0.wireOp",EDGE,"E17.MirrorCS"),sQuery(id+"F0.wireOp",EDGE,"E18.MirrorCS"),sQuery(id+"F0.wireOp",EDGE,"E19.MirrorCS"),sQuery(id+"F0.wireOp",EDGE,"E20.MirrorCS"),sQuery(id+"F0.wireOp",EDGE,"E21.MirrorCS"),sQuery(id+"F0.wireOp",EDGE,"E22.MirrorCS"),sQuery(id+"F0.wireOp",EDGE,"E23.MirrorCS"),sQuery(id+"F0.wireOp",EDGE,"E24.MirrorCS"),sQuery(id+"F0.wireOp",EDGE,"E25.MirrorCS"),sQuery(id+"F0.wireOp",EDGE,"E26.MirrorCS"),sQuery(id+"F0.wireOp",EDGE,"E27.MirrorCS")])],"isStart":false});
            var sketch = newSketch(context, id + "F26", { "sketchPlane" : qUnion([Q0])});
            skLineSegment(sketch, "E52", {"start": v(0, 193.6) * mm, "end": v(0, -267.62) * mm});
            skCircle(sketch, "E53", {"center": v(-14, -65.02) * mm, "radius": 18.96 * mm});
            skSolve(sketch);
        }
        {
            var Q0;
            Q0=sQuery(id+"F26.wireOp",VERTEX,"E53.center");
            var Q1;
            Q1=makeQuery(id+"F1.opExtrude","SWEPT_BODY",BODY,{"disambiguationData":[OSD([sQuery(id+"F0.wireOp",EDGE,"E0"),sQuery(id+"F0.wireOp",EDGE,"E1"),sQuery(id+"F0.wireOp",EDGE,"E3"),sQuery(id+"F0.wireOp",EDGE,"E4"),sQuery(id+"F0.wireOp",EDGE,"E5"),sQuery(id+"F0.wireOp",EDGE,"E6"),sQuery(id+"F0.wireOp",EDGE,"E9"),sQuery(id+"F0.wireOp",EDGE,"E10"),sQuery(id+"F0.wireOp",EDGE,"E11"),sQuery(id+"F0.wireOp",EDGE,"E12"),sQuery(id+"F0.wireOp",EDGE,"E13"),sQuery(id+"F0.wireOp",EDGE,"E14"),sQuery(id+"F0.wireOp",EDGE,"E16.MirrorCS"),sQuery(id+"F0.wireOp",EDGE,"E17.MirrorCS"),sQuery(id+"F0.wireOp",EDGE,"E18.MirrorCS"),sQuery(id+"F0.wireOp",EDGE,"E19.MirrorCS"),sQuery(id+"F0.wireOp",EDGE,"E20.MirrorCS"),sQuery(id+"F0.wireOp",EDGE,"E21.MirrorCS"),sQuery(id+"F0.wireOp",EDGE,"E22.MirrorCS"),sQuery(id+"F0.wireOp",EDGE,"E23.MirrorCS"),sQuery(id+"F0.wireOp",EDGE,"E24.MirrorCS"),sQuery(id+"F0.wireOp",EDGE,"E25.MirrorCS"),sQuery(id+"F0.wireOp",EDGE,"E26.MirrorCS"),sQuery(id+"F0.wireOp",EDGE,"E27.MirrorCS")])]});
            hole(context, id + "F27", {"style" : HoleStyle.SIMPLE, "endStyle" : HoleEndStyle.BLIND, "holeDiameter" : 5 * mm, "holeDepth" : 4 * mm, "tappedDepth" : 12 * mm, "tapClearance" : 3, "startFromSketch" : true, "locations" : qUnion([Q0]), "scope" : qUnion([Q1])});
        }
        {
            var Q0;
            Q0=makeQuery(id+"F1.opExtrude","CAP_FACE",FACE,{"disambiguationData":[OSD([sQuery(id+"F0.wireOp",EDGE,"E0"),sQuery(id+"F0.wireOp",EDGE,"E1"),sQuery(id+"F0.wireOp",EDGE,"E3"),sQuery(id+"F0.wireOp",EDGE,"E4"),sQuery(id+"F0.wireOp",EDGE,"E5"),sQuery(id+"F0.wireOp",EDGE,"E6"),sQuery(id+"F0.wireOp",EDGE,"E9"),sQuery(id+"F0.wireOp",EDGE,"E10"),sQuery(id+"F0.wireOp",EDGE,"E11"),sQuery(id+"F0.wireOp",EDGE,"E12"),sQuery(id+"F0.wireOp",EDGE,"E13"),sQuery(id+"F0.wireOp",EDGE,"E14"),sQuery(id+"F0.wireOp",EDGE,"E16.MirrorCS"),sQuery(id+"F0.wireOp",EDGE,"E17.MirrorCS"),sQuery(id+"F0.wireOp",EDGE,"E18.MirrorCS"),sQuery(id+"F0.wireOp",EDGE,"E19.MirrorCS"),sQuery(id+"F0.wireOp",EDGE,"E20.MirrorCS"),sQuery(id+"F0.wireOp",EDGE,"E21.MirrorCS"),sQuery(id+"F0.wireOp",EDGE,"E22.MirrorCS"),sQuery(id+"F0.wireOp",EDGE,"E23.MirrorCS"),sQuery(id+"F0.wireOp",EDGE,"E24.MirrorCS"),sQuery(id+"F0.wireOp",EDGE,"E25.MirrorCS"),sQuery(id+"F0.wireOp",EDGE,"E26.MirrorCS"),sQuery(id+"F0.wireOp",EDGE,"E27.MirrorCS")])],"isStart":false});
            var sketch = newSketch(context, id + "F28", { "sketchPlane" : qUnion([Q0])});
            skLineSegment(sketch, "E54", {"start": v(0, 193.6) * mm, "end": v(0, -267.62) * mm});
            skCircle(sketch, "E55", {"center": v(28, -127.62) * mm, "radius": 9.81 * mm});
            skSolve(sketch);
        }
        {
            var Q0;
            Q0=sQuery(id+"F28.wireOp",VERTEX,"E55.center");
            var Q1;
            Q1=makeQuery(id+"F1.opExtrude","SWEPT_BODY",BODY,{"disambiguationData":[OSD([sQuery(id+"F0.wireOp",EDGE,"E0"),sQuery(id+"F0.wireOp",EDGE,"E1"),sQuery(id+"F0.wireOp",EDGE,"E3"),sQuery(id+"F0.wireOp",EDGE,"E4"),sQuery(id+"F0.wireOp",EDGE,"E5"),sQuery(id+"F0.wireOp",EDGE,"E6"),sQuery(id+"F0.wireOp",EDGE,"E9"),sQuery(id+"F0.wireOp",EDGE,"E10"),sQuery(id+"F0.wireOp",EDGE,"E11"),sQuery(id+"F0.wireOp",EDGE,"E12"),sQuery(id+"F0.wireOp",EDGE,"E13"),sQuery(id+"F0.wireOp",EDGE,"E14"),sQuery(id+"F0.wireOp",EDGE,"E16.MirrorCS"),sQuery(id+"F0.wireOp",EDGE,"E17.MirrorCS"),sQuery(id+"F0.wireOp",EDGE,"E18.MirrorCS"),sQuery(id+"F0.wireOp",EDGE,"E19.MirrorCS"),sQuery(id+"F0.wireOp",EDGE,"E20.MirrorCS"),sQuery(id+"F0.wireOp",EDGE,"E21.MirrorCS"),sQuery(id+"F0.wireOp",EDGE,"E22.MirrorCS"),sQuery(id+"F0.wireOp",EDGE,"E23.MirrorCS"),sQuery(id+"F0.wireOp",EDGE,"E24.MirrorCS"),sQuery(id+"F0.wireOp",EDGE,"E25.MirrorCS"),sQuery(id+"F0.wireOp",EDGE,"E26.MirrorCS"),sQuery(id+"F0.wireOp",EDGE,"E27.MirrorCS")])]});
            hole(context, id + "F29", {"style" : HoleStyle.SIMPLE, "endStyle" : HoleEndStyle.BLIND, "holeDiameter" : 5 * mm, "holeDepth" : 4 * mm, "tappedDepth" : 12 * mm, "tapClearance" : 3, "startFromSketch" : true, "locations" : qUnion([Q0]), "scope" : qUnion([Q1])});
        }
        {
            var Q0;
            Q0=makeQuery(id+"F1.opExtrude","CAP_FACE",FACE,{"disambiguationData":[OSD([sQuery(id+"F0.wireOp",EDGE,"E0"),sQuery(id+"F0.wireOp",EDGE,"E1"),sQuery(id+"F0.wireOp",EDGE,"E3"),sQuery(id+"F0.wireOp",EDGE,"E4"),sQuery(id+"F0.wireOp",EDGE,"E5"),sQuery(id+"F0.wireOp",EDGE,"E6"),sQuery(id+"F0.wireOp",EDGE,"E9"),sQuery(id+"F0.wireOp",EDGE,"E10"),sQuery(id+"F0.wireOp",EDGE,"E11"),sQuery(id+"F0.wireOp",EDGE,"E12"),sQuery(id+"F0.wireOp",EDGE,"E13"),sQuery(id+"F0.wireOp",EDGE,"E14"),sQuery(id+"F0.wireOp",EDGE,"E16.MirrorCS"),sQuery(id+"F0.wireOp",EDGE,"E17.MirrorCS"),sQuery(id+"F0.wireOp",EDGE,"E18.MirrorCS"),sQuery(id+"F0.wireOp",EDGE,"E19.MirrorCS"),sQuery(id+"F0.wireOp",EDGE,"E20.MirrorCS"),sQuery(id+"F0.wireOp",EDGE,"E21.MirrorCS"),sQuery(id+"F0.wireOp",EDGE,"E22.MirrorCS"),sQuery(id+"F0.wireOp",EDGE,"E23.MirrorCS"),sQuery(id+"F0.wireOp",EDGE,"E24.MirrorCS"),sQuery(id+"F0.wireOp",EDGE,"E25.MirrorCS"),sQuery(id+"F0.wireOp",EDGE,"E26.MirrorCS"),sQuery(id+"F0.wireOp",EDGE,"E27.MirrorCS")])],"isStart":false});
            var sketch = newSketch(context, id + "F30", { "sketchPlane" : qUnion([Q0])});
            skLineSegment(sketch, "E56", {"start": v(0, 193.6) * mm, "end": v(0, -267.62) * mm});
            skCircle(sketch, "E57", {"center": v(20, -141.62) * mm, "radius": 14.01 * mm});
            skSolve(sketch);
        }
        {
            var Q0;
            Q0=sQuery(id+"F30.wireOp",VERTEX,"E57.center");
            var Q1;
            Q1=makeQuery(id+"F1.opExtrude","SWEPT_BODY",BODY,{"disambiguationData":[OSD([sQuery(id+"F0.wireOp",EDGE,"E0"),sQuery(id+"F0.wireOp",EDGE,"E1"),sQuery(id+"F0.wireOp",EDGE,"E3"),sQuery(id+"F0.wireOp",EDGE,"E4"),sQuery(id+"F0.wireOp",EDGE,"E5"),sQuery(id+"F0.wireOp",EDGE,"E6"),sQuery(id+"F0.wireOp",EDGE,"E9"),sQuery(id+"F0.wireOp",EDGE,"E10"),sQuery(id+"F0.wireOp",EDGE,"E11"),sQuery(id+"F0.wireOp",EDGE,"E12"),sQuery(id+"F0.wireOp",EDGE,"E13"),sQuery(id+"F0.wireOp",EDGE,"E14"),sQuery(id+"F0.wireOp",EDGE,"E16.MirrorCS"),sQuery(id+"F0.wireOp",EDGE,"E17.MirrorCS"),sQuery(id+"F0.wireOp",EDGE,"E18.MirrorCS"),sQuery(id+"F0.wireOp",EDGE,"E19.MirrorCS"),sQuery(id+"F0.wireOp",EDGE,"E20.MirrorCS"),sQuery(id+"F0.wireOp",EDGE,"E21.MirrorCS"),sQuery(id+"F0.wireOp",EDGE,"E22.MirrorCS"),sQuery(id+"F0.wireOp",EDGE,"E23.MirrorCS"),sQuery(id+"F0.wireOp",EDGE,"E24.MirrorCS"),sQuery(id+"F0.wireOp",EDGE,"E25.MirrorCS"),sQuery(id+"F0.wireOp",EDGE,"E26.MirrorCS"),sQuery(id+"F0.wireOp",EDGE,"E27.MirrorCS")])]});
            hole(context, id + "F31", {"style" : HoleStyle.SIMPLE, "endStyle" : HoleEndStyle.BLIND, "holeDiameter" : 8 * mm, "holeDepth" : 4 * mm, "tappedDepth" : 12 * mm, "tapClearance" : 3, "startFromSketch" : true, "locations" : qUnion([Q0]), "scope" : qUnion([Q1])});
        }
        {
            var Q0;
            Q0=makeQuery(id+"F1.opExtrude","CAP_FACE",FACE,{"disambiguationData":[OSD([sQuery(id+"F0.wireOp",EDGE,"E0"),sQuery(id+"F0.wireOp",EDGE,"E1"),sQuery(id+"F0.wireOp",EDGE,"E3"),sQuery(id+"F0.wireOp",EDGE,"E4"),sQuery(id+"F0.wireOp",EDGE,"E5"),sQuery(id+"F0.wireOp",EDGE,"E6"),sQuery(id+"F0.wireOp",EDGE,"E9"),sQuery(id+"F0.wireOp",EDGE,"E10"),sQuery(id+"F0.wireOp",EDGE,"E11"),sQuery(id+"F0.wireOp",EDGE,"E12"),sQuery(id+"F0.wireOp",EDGE,"E13"),sQuery(id+"F0.wireOp",EDGE,"E14"),sQuery(id+"F0.wireOp",EDGE,"E16.MirrorCS"),sQuery(id+"F0.wireOp",EDGE,"E17.MirrorCS"),sQuery(id+"F0.wireOp",EDGE,"E18.MirrorCS"),sQuery(id+"F0.wireOp",EDGE,"E19.MirrorCS"),sQuery(id+"F0.wireOp",EDGE,"E20.MirrorCS"),sQuery(id+"F0.wireOp",EDGE,"E21.MirrorCS"),sQuery(id+"F0.wireOp",EDGE,"E22.MirrorCS"),sQuery(id+"F0.wireOp",EDGE,"E23.MirrorCS"),sQuery(id+"F0.wireOp",EDGE,"E24.MirrorCS"),sQuery(id+"F0.wireOp",EDGE,"E25.MirrorCS"),sQuery(id+"F0.wireOp",EDGE,"E26.MirrorCS"),sQuery(id+"F0.wireOp",EDGE,"E27.MirrorCS")])],"isStart":false});
            var sketch = newSketch(context, id + "F32", { "sketchPlane" : qUnion([Q0])});
            skLineSegment(sketch, "E58", {"start": v(0, 193.6) * mm, "end": v(0, -267.62) * mm});
            skCircle(sketch, "E59", {"center": v(-20, -141.62) * mm, "radius": 20.64 * mm});
            skSolve(sketch);
        }
        {
            var Q0;
            Q0=sQuery(id+"F32.wireOp",VERTEX,"E59.center");
            var Q1;
            Q1=makeQuery(id+"F1.opExtrude","SWEPT_BODY",BODY,{"disambiguationData":[OSD([sQuery(id+"F0.wireOp",EDGE,"E0"),sQuery(id+"F0.wireOp",EDGE,"E1"),sQuery(id+"F0.wireOp",EDGE,"E3"),sQuery(id+"F0.wireOp",EDGE,"E4"),sQuery(id+"F0.wireOp",EDGE,"E5"),sQuery(id+"F0.wireOp",EDGE,"E6"),sQuery(id+"F0.wireOp",EDGE,"E9"),sQuery(id+"F0.wireOp",EDGE,"E10"),sQuery(id+"F0.wireOp",EDGE,"E11"),sQuery(id+"F0.wireOp",EDGE,"E12"),sQuery(id+"F0.wireOp",EDGE,"E13"),sQuery(id+"F0.wireOp",EDGE,"E14"),sQuery(id+"F0.wireOp",EDGE,"E16.MirrorCS"),sQuery(id+"F0.wireOp",EDGE,"E17.MirrorCS"),sQuery(id+"F0.wireOp",EDGE,"E18.MirrorCS"),sQuery(id+"F0.wireOp",EDGE,"E19.MirrorCS"),sQuery(id+"F0.wireOp",EDGE,"E20.MirrorCS"),sQuery(id+"F0.wireOp",EDGE,"E21.MirrorCS"),sQuery(id+"F0.wireOp",EDGE,"E22.MirrorCS"),sQuery(id+"F0.wireOp",EDGE,"E23.MirrorCS"),sQuery(id+"F0.wireOp",EDGE,"E24.MirrorCS"),sQuery(id+"F0.wireOp",EDGE,"E25.MirrorCS"),sQuery(id+"F0.wireOp",EDGE,"E26.MirrorCS"),sQuery(id+"F0.wireOp",EDGE,"E27.MirrorCS")])]});
            hole(context, id + "F33", {"style" : HoleStyle.SIMPLE, "endStyle" : HoleEndStyle.BLIND, "holeDiameter" : 8 * mm, "holeDepth" : 4 * mm, "tappedDepth" : 12 * mm, "tapClearance" : 3, "startFromSketch" : true, "locations" : qUnion([Q0]), "scope" : qUnion([Q1])});
        }
        {
            var Q0;
            Q0=makeQuery(id+"F1.opExtrude","CAP_FACE",FACE,{"disambiguationData":[OSD([sQuery(id+"F0.wireOp",EDGE,"E0"),sQuery(id+"F0.wireOp",EDGE,"E1"),sQuery(id+"F0.wireOp",EDGE,"E3"),sQuery(id+"F0.wireOp",EDGE,"E4"),sQuery(id+"F0.wireOp",EDGE,"E5"),sQuery(id+"F0.wireOp",EDGE,"E6"),sQuery(id+"F0.wireOp",EDGE,"E9"),sQuery(id+"F0.wireOp",EDGE,"E10"),sQuery(id+"F0.wireOp",EDGE,"E11"),sQuery(id+"F0.wireOp",EDGE,"E12"),sQuery(id+"F0.wireOp",EDGE,"E13"),sQuery(id+"F0.wireOp",EDGE,"E14"),sQuery(id+"F0.wireOp",EDGE,"E16.MirrorCS"),sQuery(id+"F0.wireOp",EDGE,"E17.MirrorCS"),sQuery(id+"F0.wireOp",EDGE,"E18.MirrorCS"),sQuery(id+"F0.wireOp",EDGE,"E19.MirrorCS"),sQuery(id+"F0.wireOp",EDGE,"E20.MirrorCS"),sQuery(id+"F0.wireOp",EDGE,"E21.MirrorCS"),sQuery(id+"F0.wireOp",EDGE,"E22.MirrorCS"),sQuery(id+"F0.wireOp",EDGE,"E23.MirrorCS"),sQuery(id+"F0.wireOp",EDGE,"E24.MirrorCS"),sQuery(id+"F0.wireOp",EDGE,"E25.MirrorCS"),sQuery(id+"F0.wireOp",EDGE,"E26.MirrorCS"),sQuery(id+"F0.wireOp",EDGE,"E27.MirrorCS")])],"isStart":false});
            var sketch = newSketch(context, id + "F34", { "sketchPlane" : qUnion([Q0])});
            skLineSegment(sketch, "E60", {"start": v(0, 193.6) * mm, "end": v(0, -267.62) * mm});
            skCircle(sketch, "E61", {"center": v(-17.5, -157.62) * mm, "radius": 18.06 * mm});
            skSolve(sketch);
        }
        {
            var Q0;
            Q0=sQuery(id+"F34.wireOp",VERTEX,"E61.center");
            var Q1;
            Q1=makeQuery(id+"F1.opExtrude","SWEPT_BODY",BODY,{"disambiguationData":[OSD([sQuery(id+"F0.wireOp",EDGE,"E0"),sQuery(id+"F0.wireOp",EDGE,"E1"),sQuery(id+"F0.wireOp",EDGE,"E3"),sQuery(id+"F0.wireOp",EDGE,"E4"),sQuery(id+"F0.wireOp",EDGE,"E5"),sQuery(id+"F0.wireOp",EDGE,"E6"),sQuery(id+"F0.wireOp",EDGE,"E9"),sQuery(id+"F0.wireOp",EDGE,"E10"),sQuery(id+"F0.wireOp",EDGE,"E11"),sQuery(id+"F0.wireOp",EDGE,"E12"),sQuery(id+"F0.wireOp",EDGE,"E13"),sQuery(id+"F0.wireOp",EDGE,"E14"),sQuery(id+"F0.wireOp",EDGE,"E16.MirrorCS"),sQuery(id+"F0.wireOp",EDGE,"E17.MirrorCS"),sQuery(id+"F0.wireOp",EDGE,"E18.MirrorCS"),sQuery(id+"F0.wireOp",EDGE,"E19.MirrorCS"),sQuery(id+"F0.wireOp",EDGE,"E20.MirrorCS"),sQuery(id+"F0.wireOp",EDGE,"E21.MirrorCS"),sQuery(id+"F0.wireOp",EDGE,"E22.MirrorCS"),sQuery(id+"F0.wireOp",EDGE,"E23.MirrorCS"),sQuery(id+"F0.wireOp",EDGE,"E24.MirrorCS"),sQuery(id+"F0.wireOp",EDGE,"E25.MirrorCS"),sQuery(id+"F0.wireOp",EDGE,"E26.MirrorCS"),sQuery(id+"F0.wireOp",EDGE,"E27.MirrorCS")])]});
            hole(context, id + "F35", {"style" : HoleStyle.SIMPLE, "endStyle" : HoleEndStyle.BLIND, "holeDiameter" : 3.5 * mm, "holeDepth" : 4 * mm, "tappedDepth" : 12 * mm, "tapClearance" : 3, "startFromSketch" : true, "locations" : qUnion([Q0]), "scope" : qUnion([Q1])});
        }
        {
            var Q0;
            Q0=makeQuery(id+"F1.opExtrude","CAP_FACE",FACE,{"disambiguationData":[OSD([sQuery(id+"F0.wireOp",EDGE,"E0"),sQuery(id+"F0.wireOp",EDGE,"E1"),sQuery(id+"F0.wireOp",EDGE,"E3"),sQuery(id+"F0.wireOp",EDGE,"E4"),sQuery(id+"F0.wireOp",EDGE,"E5"),sQuery(id+"F0.wireOp",EDGE,"E6"),sQuery(id+"F0.wireOp",EDGE,"E9"),sQuery(id+"F0.wireOp",EDGE,"E10"),sQuery(id+"F0.wireOp",EDGE,"E11"),sQuery(id+"F0.wireOp",EDGE,"E12"),sQuery(id+"F0.wireOp",EDGE,"E13"),sQuery(id+"F0.wireOp",EDGE,"E14"),sQuery(id+"F0.wireOp",EDGE,"E16.MirrorCS"),sQuery(id+"F0.wireOp",EDGE,"E17.MirrorCS"),sQuery(id+"F0.wireOp",EDGE,"E18.MirrorCS"),sQuery(id+"F0.wireOp",EDGE,"E19.MirrorCS"),sQuery(id+"F0.wireOp",EDGE,"E20.MirrorCS"),sQuery(id+"F0.wireOp",EDGE,"E21.MirrorCS"),sQuery(id+"F0.wireOp",EDGE,"E22.MirrorCS"),sQuery(id+"F0.wireOp",EDGE,"E23.MirrorCS"),sQuery(id+"F0.wireOp",EDGE,"E24.MirrorCS"),sQuery(id+"F0.wireOp",EDGE,"E25.MirrorCS"),sQuery(id+"F0.wireOp",EDGE,"E26.MirrorCS"),sQuery(id+"F0.wireOp",EDGE,"E27.MirrorCS")])],"isStart":false});
            var sketch = newSketch(context, id + "F36", { "sketchPlane" : qUnion([Q0])});
            skLineSegment(sketch, "E62", {"start": v(0, 193.6) * mm, "end": v(0, -267.62) * mm});
            skCircle(sketch, "E63", {"center": v(17.5, -157.62) * mm, "radius": 15.02 * mm});
            skSolve(sketch);
        }
        {
            var Q0;
            Q0=sQuery(id+"F36.wireOp",VERTEX,"E63.center");
            var Q1;
            Q1=makeQuery(id+"F1.opExtrude","SWEPT_BODY",BODY,{"disambiguationData":[OSD([sQuery(id+"F0.wireOp",EDGE,"E0"),sQuery(id+"F0.wireOp",EDGE,"E1"),sQuery(id+"F0.wireOp",EDGE,"E3"),sQuery(id+"F0.wireOp",EDGE,"E4"),sQuery(id+"F0.wireOp",EDGE,"E5"),sQuery(id+"F0.wireOp",EDGE,"E6"),sQuery(id+"F0.wireOp",EDGE,"E9"),sQuery(id+"F0.wireOp",EDGE,"E10"),sQuery(id+"F0.wireOp",EDGE,"E11"),sQuery(id+"F0.wireOp",EDGE,"E12"),sQuery(id+"F0.wireOp",EDGE,"E13"),sQuery(id+"F0.wireOp",EDGE,"E14"),sQuery(id+"F0.wireOp",EDGE,"E16.MirrorCS"),sQuery(id+"F0.wireOp",EDGE,"E17.MirrorCS"),sQuery(id+"F0.wireOp",EDGE,"E18.MirrorCS"),sQuery(id+"F0.wireOp",EDGE,"E19.MirrorCS"),sQuery(id+"F0.wireOp",EDGE,"E20.MirrorCS"),sQuery(id+"F0.wireOp",EDGE,"E21.MirrorCS"),sQuery(id+"F0.wireOp",EDGE,"E22.MirrorCS"),sQuery(id+"F0.wireOp",EDGE,"E23.MirrorCS"),sQuery(id+"F0.wireOp",EDGE,"E24.MirrorCS"),sQuery(id+"F0.wireOp",EDGE,"E25.MirrorCS"),sQuery(id+"F0.wireOp",EDGE,"E26.MirrorCS"),sQuery(id+"F0.wireOp",EDGE,"E27.MirrorCS")])]});
            hole(context, id + "F37", {"style" : HoleStyle.SIMPLE, "endStyle" : HoleEndStyle.BLIND, "holeDiameter" : 3.5 * mm, "holeDepth" : 4 * mm, "tappedDepth" : 12 * mm, "tapClearance" : 3, "startFromSketch" : true, "locations" : qUnion([Q0]), "scope" : qUnion([Q1])});
        }
    });
